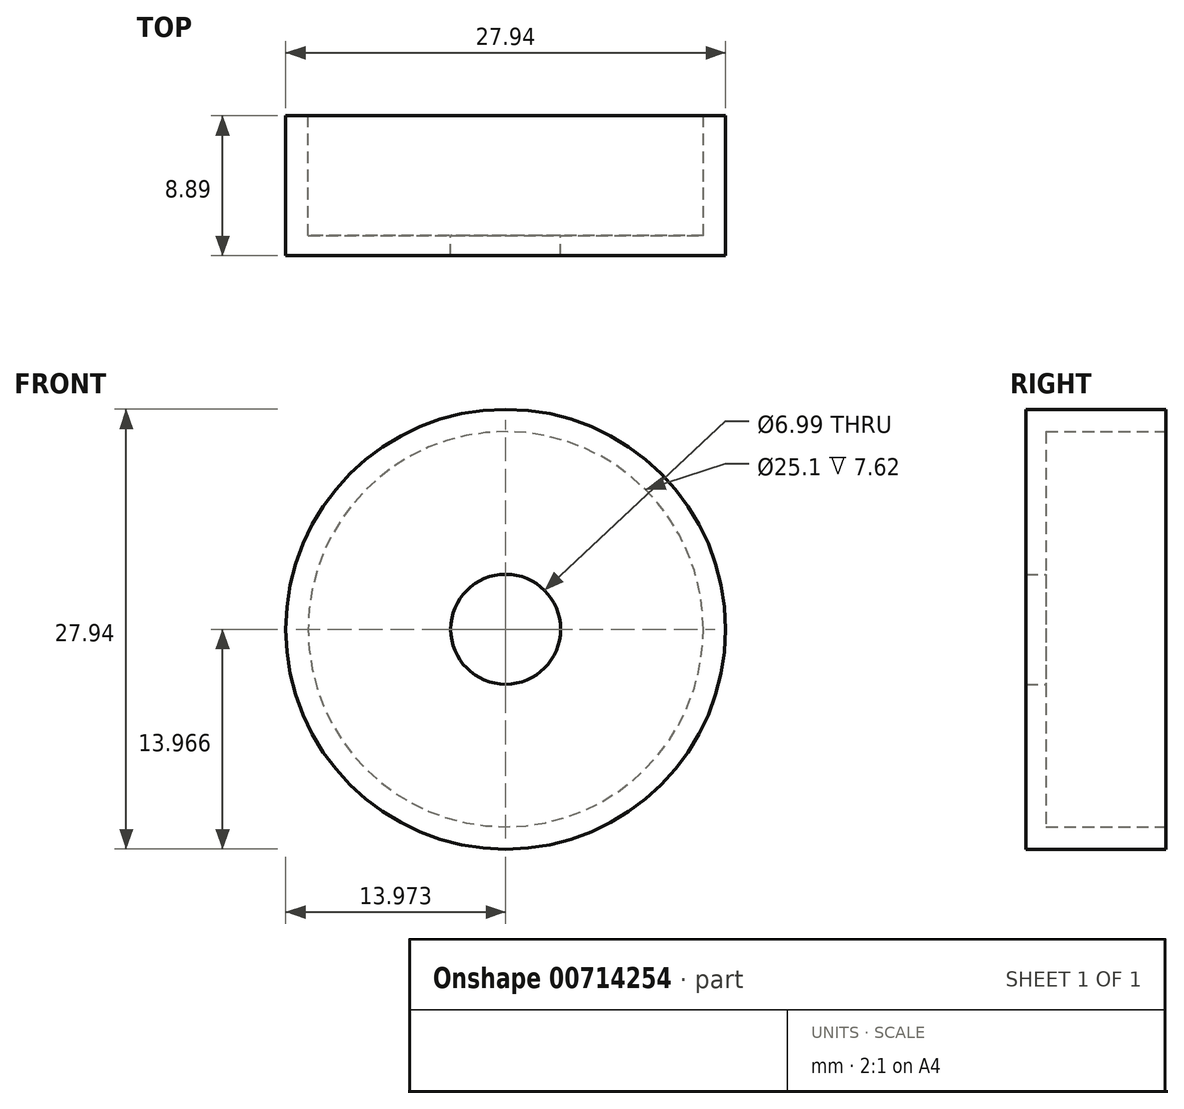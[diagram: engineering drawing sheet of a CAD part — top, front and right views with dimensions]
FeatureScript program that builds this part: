
annotation { "Feature Type Name" : "Feature", "Feature Type Description" : "" }
export const myFeature = defineFeature(function(context is Context, id is Id, definition is map)
    precondition{}
    {
        {
            var Q0;
            Q0=qCreatedBy(makeId("Front.planeOp"),FACE);
            var sketch = newSketch(context, id + "F0", { "sketchPlane" : qUnion([Q0])});
            skCircle(sketch, "E0", {"center": v(-132.36, 62.63) * mm, "radius": 13.97 * mm});
            skCircle(sketch, "E1", {"center": v(-132.36, 62.63) * mm, "radius": 3.5 * mm});
            skSolve(sketch);
        }
        {
            var Q0;
            Q0 = qSketchRegion(id + "F0", true);
            extrude(context, id + "F1", {"entities" : qUnion([Q0]), "depth" : 8.9 * mm, "offsetDistance" : 25.4 * mm});
        }
        {
            var Q0;
            Q0=makeQuery(id+"F1.opExtrude","CAP_FACE",FACE,{"disambiguationData":[OSD([sQuery(id+"F0.wireOp",EDGE,"E0"),sQuery(id+"F0.wireOp",EDGE,"E1")])],"isStart":true});
            var sketch = newSketch(context, id + "F2", { "sketchPlane" : qUnion([Q0])});
            skCircle(sketch, "E2", {"center": v(132.36, 62.63) * mm, "radius": 12.55 * mm});
            skSolve(sketch);
        }
        {
            var Q0;
            Q0 = qSketchRegion(id + "F2", true);
            extrude(context, id + "F3", {"entities" : qUnion([Q0]), "operationType" : NewBodyOperationType.REMOVE, "oppositeDirection" : true, "depth" : 7.62 * mm, "offsetDistance" : 25.4 * mm});
        }
    });
